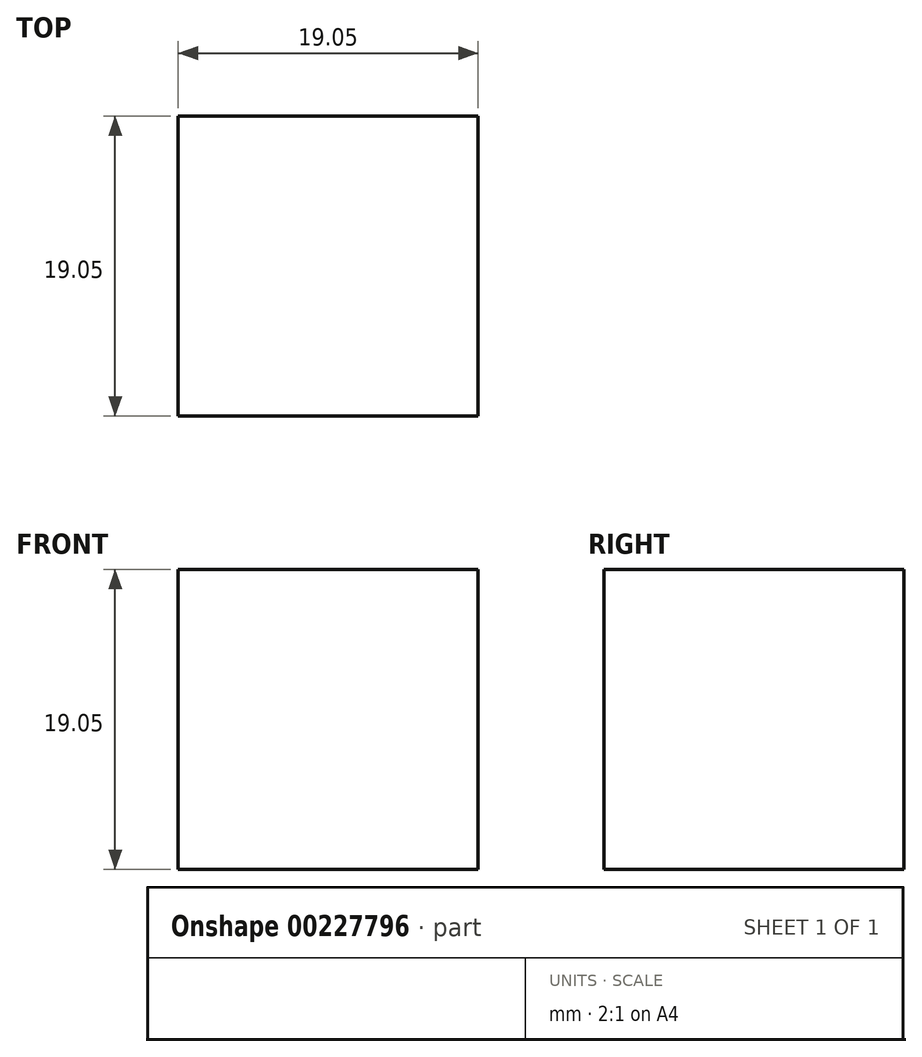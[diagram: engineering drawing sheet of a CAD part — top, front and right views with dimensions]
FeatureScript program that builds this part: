
annotation { "Feature Type Name" : "Feature", "Feature Type Description" : "" }
export const myFeature = defineFeature(function(context is Context, id is Id, definition is map)
    precondition{}
    {
        {
            var Q0;
            Q0=qCreatedBy(makeId("Front.planeOp"),FACE);
            var sketch = newSketch(context, id + "F0", { "sketchPlane" : qUnion([Q0])});
            skLineSegment(sketch, "E0.bottom", {"start": v(-40.12, 38.48) * mm, "end": v(-21.07, 38.48) * mm});
            skLineSegment(sketch, "E0.top", {"start": v(-40.12, 19.43) * mm, "end": v(-21.07, 19.43) * mm});
            skLineSegment(sketch, "E0.left", {"start": v(-40.12, 38.48) * mm, "end": v(-40.12, 19.43) * mm});
            skLineSegment(sketch, "E0.right", {"start": v(-21.07, 38.48) * mm, "end": v(-21.07, 19.43) * mm});
            skSolve(sketch);
        }
        {
            var Q0;
            Q0=makeQuery(id+"F0.imprint","IMPRINT",FACE,{"disambiguationData":[TD([[makeQuery(id+"F0.imprint","IMPRINT",EDGE,{"derivedFrom":sQuery(id+"F0.wireOp",EDGE,"E0.bottom")}),-1.0]])]});
            extrude(context, id + "F1", {"entities" : qUnion([Q0]), "depth" : 19.05 * mm});
        }
    });
